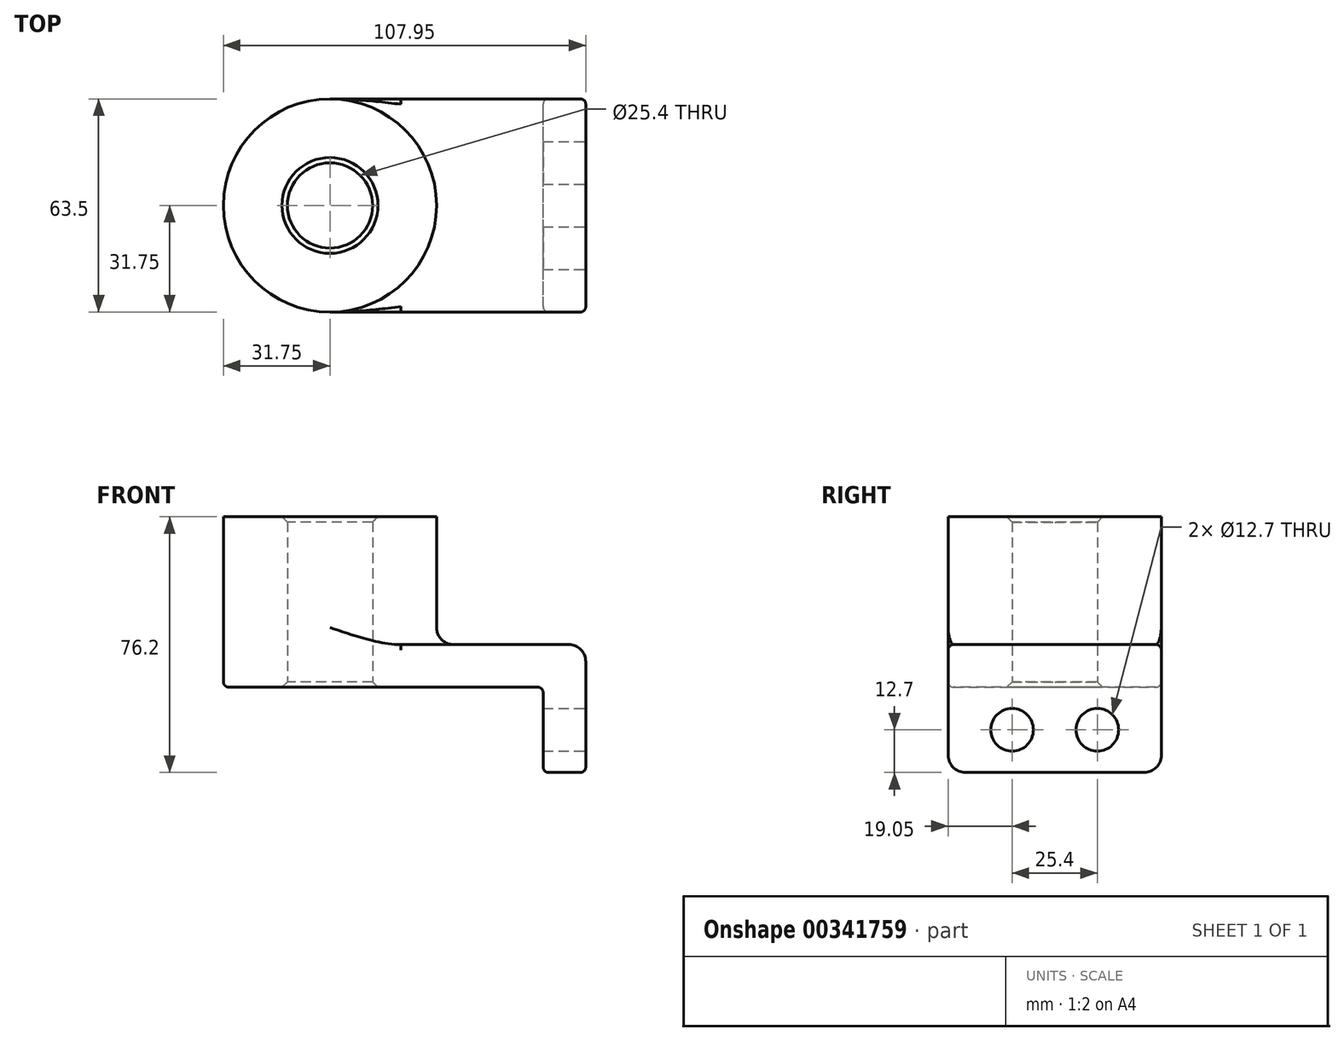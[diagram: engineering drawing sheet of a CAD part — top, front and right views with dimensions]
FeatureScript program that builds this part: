
annotation { "Feature Type Name" : "Feature", "Feature Type Description" : "" }
export const myFeature = defineFeature(function(context is Context, id is Id, definition is map)
    precondition{}
    {
        {
            var Q0;
            Q0=qCreatedBy(makeId("Top.planeOp"),FACE);
            var sketch = newSketch(context, id + "F0", { "sketchPlane" : qUnion([Q0])});
            skLineSegment(sketch, "E0.bottom", {"start": v(38.1, -31.75) * mm, "end": v(-38.1, -31.75) * mm});
            skLineSegment(sketch, "E0.top", {"start": v(38.1, 31.75) * mm, "end": v(-38.1, 31.75) * mm});
            skLineSegment(sketch, "E0.left", {"start": v(38.1, -31.75) * mm, "end": v(38.1, 31.75) * mm});
            skLineSegment(sketch, "E0.right", {"start": v(-38.1, -31.75) * mm, "end": v(-38.1, 31.75) * mm});
            skPoint(sketch, "E0.middle", {"position": v(0, 0) * mm});
            skCircle(sketch, "E1", {"center": v(-38.1, 0) * mm, "radius": 31.75 * mm});
            skCircle(sketch, "E2", {"center": v(-38.1, 0) * mm, "radius": 12.7 * mm});
            skSolve(sketch);
        }
        {
            var Q0;
            Q0 = qSketchRegion(id + "F0", true);
            extrude(context, id + "F1", {"entities" : qUnion([Q0]), "depth" : 12.7 * mm});
        }
        {
            var Q0;
            {var subQ1=sQuery(id+"F0.wireOp",EDGE,"E0.right");var subQ3=sQuery(id+"F0.wireOp",EDGE,"E2");var subQ4=makeQuery(id+"F0.imprint","INTERSECT",VERTEX,{"disambiguationData":[OD(0.0)],"derivedFrom":[subQ1,subQ3]});Q0=makeQuery(id+"F0.imprint","IMPRINT",FACE,{"disambiguationData":[TD([[makeQuery(id+"F0.imprint","IMPRINT",EDGE,{"disambiguationData":[TD([[subQ4,-1.0]])],"derivedFrom":subQ3}),-1.0]])]});}
            var Q1;
            {var subQ1=sQuery(id+"F0.wireOp",EDGE,"E0.right");var subQ3=sQuery(id+"F0.wireOp",EDGE,"E2");var subQ4=makeQuery(id+"F0.imprint","INTERSECT",VERTEX,{"disambiguationData":[OD(0.0)],"derivedFrom":[subQ1,subQ3]});Q1=makeQuery(id+"F0.imprint","IMPRINT",FACE,{"disambiguationData":[TD([[makeQuery(id+"F0.imprint","IMPRINT",EDGE,{"disambiguationData":[TD([[subQ4,1.0]])],"derivedFrom":subQ3}),-1.0]])]});}
            extrude(context, id + "F2", {"entities" : qUnion([Q0, Q1]), "operationType" : NewBodyOperationType.ADD, "depth" : 50.8 * mm});
        }
        {
            var Q0;
            Q0=makeQuery(id+"F1.opExtrude","SWEPT_FACE",FACE,{"disambiguationData":[OSD([sQuery(id+"F0.wireOp",EDGE,"E0.left")])]});
            var sketch = newSketch(context, id + "F3", { "sketchPlane" : qUnion([Q0])});
            skLineSegment(sketch, "E3.bottom", {"start": v(-31.75, 12.7) * mm, "end": v(31.75, 12.7) * mm});
            skLineSegment(sketch, "E3.top", {"start": v(-31.75, -25.4) * mm, "end": v(31.75, -25.4) * mm});
            skLineSegment(sketch, "E3.left", {"start": v(-31.75, 12.7) * mm, "end": v(-31.75, -25.4) * mm});
            skLineSegment(sketch, "E3.right", {"start": v(31.75, 12.7) * mm, "end": v(31.75, -25.4) * mm});
            skLineSegment(sketch, "E4", {"start": v(0, 0) * mm, "end": v(0, -25.4) * mm});
            skCircle(sketch, "E5", {"center": v(-12.7, -12.7) * mm, "radius": 6.35 * mm});
            skCircle(sketch, "E6.MirrorC", {"center": v(12.7, -12.7) * mm, "radius": 6.35 * mm});
            skSolve(sketch);
        }
        {
            var Q0;
            Q0 = qSketchRegion(id + "F3", true);
            extrude(context, id + "F4", {"entities" : qUnion([Q0]), "operationType" : NewBodyOperationType.ADD, "oppositeDirection" : true, "depth" : 12.7 * mm});
        }
        {
            var Q0;
            {var subQ0=sQuery(id+"F0.wireOp",EDGE,"E1");Q0=makeQuery(id+"F2.boolean.opBoolean","INTERSECT",EDGE,{"derivedFrom":[makeQuery(id+"F1.opExtrude","CAP_FACE",FACE,{"disambiguationData":[OSD([sQuery(id+"F0.wireOp",EDGE,"E0.bottom"),sQuery(id+"F0.wireOp",EDGE,"E0.top"),sQuery(id+"F0.wireOp",EDGE,"E0.left"),subQ0,sQuery(id+"F0.wireOp",EDGE,"E2")])],"isStart":false}),makeQuery(id+"F2.opExtrude","SWEPT_FACE",FACE,{"disambiguationData":[OSD([subQ0])]})]});}
            var Q1;
            Q1=makeQuery(id+"F1.opExtrude","CAP_EDGE",EDGE,{"disambiguationData":[OSD([sQuery(id+"F0.wireOp",EDGE,"E0.left")])],"isStart":false});
            var Q2;
            Q2=makeQuery(id+"F4.opExtrude","SWEPT_EDGE",EDGE,{"disambiguationData":[OSD([sQuery(id+"F3.wireOp",EDGE,"E3.top"),sQuery(id+"F3.wireOp",EDGE,"E3.left")])]});
            var Q3;
            Q3=makeQuery(id+"F4.opExtrude","SWEPT_EDGE",EDGE,{"disambiguationData":[OSD([sQuery(id+"F3.wireOp",EDGE,"E3.top"),sQuery(id+"F3.wireOp",EDGE,"E3.right")])]});
            fillet(context, id + "F5", {"entities" : qUnion([Q0, Q1, Q2, Q3]), "radius" : 5.08 * mm, "tangentPropagation" : true, "allowEdgeOverflow" : false});
        }
        {
            var Q0;
            Q0=makeQuery(id+"F1.opExtrude","CAP_EDGE",EDGE,{"disambiguationData":[OSD([sQuery(id+"F0.wireOp",EDGE,"E0.bottom")])],"isStart":false});
            var Q1;
            Q1=makeQuery(id+"F1.opExtrude","CAP_EDGE",EDGE,{"disambiguationData":[OSD([sQuery(id+"F0.wireOp",EDGE,"E0.top")])],"isStart":false});
            var Q2;
            Q2=makeQuery(id+"F4.boolean.opBoolean","INTERSECT",EDGE,{"derivedFrom":[makeQuery(id+"F1.opExtrude","CAP_FACE",FACE,{"disambiguationData":[OSD([sQuery(id+"F0.wireOp",EDGE,"E0.bottom"),sQuery(id+"F0.wireOp",EDGE,"E0.top"),sQuery(id+"F0.wireOp",EDGE,"E0.left"),sQuery(id+"F0.wireOp",EDGE,"E1"),sQuery(id+"F0.wireOp",EDGE,"E2")])],"isStart":true}),makeQuery(id+"F4.opExtrude","CAP_FACE",FACE,{"disambiguationData":[OSD([sQuery(id+"F3.wireOp",EDGE,"E3.bottom"),sQuery(id+"F3.wireOp",EDGE,"E3.top"),sQuery(id+"F3.wireOp",EDGE,"E3.left"),sQuery(id+"F3.wireOp",EDGE,"E3.right"),sQuery(id+"F3.wireOp",EDGE,"E5"),sQuery(id+"F3.wireOp",EDGE,"E6.MirrorC")])],"isStart":false})]});
            fillet(context, id + "F6", {"entities" : qUnion([Q0, Q1, Q2]), "radius" : 1.59 * mm, "tangentPropagation" : true, "allowEdgeOverflow" : false});
        }
        {
            var Q0;
            Q0=makeQuery(id+"F1.opExtrude","CAP_EDGE",EDGE,{"disambiguationData":[OSD([sQuery(id+"F0.wireOp",EDGE,"E0.bottom")])],"isStart":true});
            fillet(context, id + "F7", {"entities" : qUnion([Q0]), "radius" : 1.59 * mm, "tangentPropagation" : true, "allowEdgeOverflow" : false});
        }
        {
            var Q0;
            {var subQ0=sQuery(id+"F0.wireOp",EDGE,"E2");Q0=makeQuery(id+"F2.boolean.opBoolean","MERGE",FACE,{"derivedFrom":[makeQuery(id+"F1.opExtrude","SWEPT_FACE",FACE,{"disambiguationData":[OSD([subQ0])]}),makeQuery(id+"F2.opExtrude","SWEPT_FACE",FACE,{"disambiguationData":[OSD([subQ0])]})]});}
            chamfer(context, id + "F8", {"entities" : qUnion([Q0]), "width" : 1.59 * mm, "tangentPropagation" : true});
        }
    });
